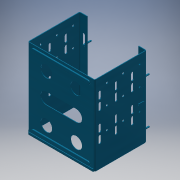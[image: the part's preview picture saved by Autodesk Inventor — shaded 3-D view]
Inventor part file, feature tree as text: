
AUTODESK INVENTOR PART (.ipt)
format: ipt  version: 2019 (Build 230136000, 136)  size: 597,504 bytes
history: native  units: mm
features: sheet_metal_op x16, sketch x14, other x12, pattern_linear x2, chamfer x1, hole x1, mirror x1
ambient origin geometry x8: Origin, YZ Plane, XZ Plane, XY Plane, X Axis, Y Axis, Z Axis, Center Point
bodies: Solid1 (feature_tree)
feature tree (47):
  parser-record x1  (decoder bookkeeping rows leaked as tree rows — omitted from the tree; the rows remain in map.json)
  sheet_metal_op  "Face1"
  sheet_metal_op  "Flange1"
  sheet_metal_op  "Hem1"
  sheet_metal_op  "Hem2"
  sheet_metal_op  "Hem3"
  sheet_metal_op  "Flange2"
  sheet_metal_op  "Flange3"
  sheet_metal_op  "Flange4"
  chamfer  "Corner Round1"
  pattern_linear  "Rectangular Pattern1"  Count1=8 Spacing1=90.0deg
  hole  "Hole1"  [1 undecoded]
  pattern_linear  "Rectangular Pattern2"  Spacing1=76.0mm  [1 undecoded]
  mirror  "Mirror1"
  sketch  "Sketch1"  dims[d1=123.0mm]
  other  "Plate1"
  sketch  "Sketch2"  dims[d3=61.5mm]
  other  "Plate2"
  sheet_metal_op  "Bend1"
  sheet_metal_op  "Corner1"
  sketch  "Sketch6"  dims[d7=0.5mm]
  other  "Plate3"
  sheet_metal_op  "Bend2"
  sheet_metal_op  "Corner2"
  sketch  "Sketch7"  dims[d8=2.0mm]
  other  "Plate4"
  sheet_metal_op  "Bend3"
  sheet_metal_op  "Corner3"
  sketch  "Sketch8"  dims[d9=1.0mm d10=80.0mm d11=90.0deg d12=1.0mm]
  sketch  "Sketch9"  dims[d13=4.0mm d14=1.0mm]
  other  "Plate5"
  sheet_metal_op  "Bend4"
  sheet_metal_op  "Corner4"
  sketch  "Sketch10"  dims[d15=1.0mm]
  sketch  "Sketch11"  dims[d16=1.0mm]
  sketch  "Sketch12"  dims[d17=0.5mm]
  sketch  "Sketch13"  dims[d18=2.0mm]
  sketch  "Sketch14"  dims[d19=1.0mm d20=76.0mm d21=2.0mm d22=4.0mm d23=0.1mm d24=0.05mm d25=1.0mm d26=0.5mm d27=2.0mm d28=1.0mm d29=76.0mm d30=2.0mm d31=4.0mm d32=0.1mm d33=0.05mm d34=1.0mm d35=0.5mm d36=2.0mm d37=1.0mm d38=4.0mm d39=0.1mm d40=0.05mm d41=1.0mm d42=0.5mm d43=2.0mm d44=1.0mm d46=90.0deg d47=1.0mm d48=4.0mm d49=1.0mm d50=1.0mm d51=1.0mm d52=0.5mm d53=2.0mm d54=1.0mm d55=12.0mm d56=90.0deg d57=1.0mm d58=4.0mm d59=1.0mm d60=1.0mm d61=12.0mm d62=4.0mm d63=-0.5mm d64=13.0mm d65=1.0mm d66=0.0mm d67=1.0mm d68=0.5mm d69=2.0mm d70=1.0mm d71=12.0mm d72=90.0deg d73=0.2mm d74=4.0mm d75=1.0mm d76=1.0mm d77=1.0mm d78=20.0mm d80=70.0mm d81=20.0mm d83=99.0mm d84=18.0mm d85=23.0mm d86=36.0mm d87=18.0mm d88=46.0mm d89=20.0mm d91=46.0mm d92=10.0mm d94=10.0mm d96=10.0mm d98=10.0mm d99=20.0mm d101=72.0mm d103=10.0mm d105=10.0mm d106=20.0mm d108=72.0mm d110=1.0mm d111=0.0mm d112=7.0mm d113=7.0mm d116=3.0mm d117=45.0mm d118=0.0mm d119=6.5mm d120=56.0mm d123=10.0mm d124=4.0mm d125=90.0deg d126=20.0mm d127=24.0mm d128=20.0mm d129=20.0mm d130=20.0mm d131=15.0mm d132=29.0mm d133=15.0mm d136=90.0deg d137=9.0mm d138=13.0mm d139=9.0mm d140=9.0mm d144=33.0mm d146=30.0mm d147=3.0mm d148=3.0mm d149=4.0mm d150=2.0mm d151=90.0deg d152=1.0mm d153=20.594885mm d154=30.0mm d156=25.0mm]
  other  "Cut1"
  other  "Cut2"
  other  "iFeature10:1"
  other  "iFeature11:1"
  other  "iFeature1:1"
  sketch  "Sketch3"  dims[d4=1.0mm]
  sketch  "Sketch4"  dims[d5=1.0mm]
  sketch  "Sketch5"  dims[d6=1.0mm]
  other  "Definition1"
note: 2 required parameter values undecoded (feature->parameter linkage not recoverable at this tier; creation-order binding heuristic only, values carry confidence <= 0.55)
note: 1 file-system path scrubbed to <path> (originals preserved in map.json)
